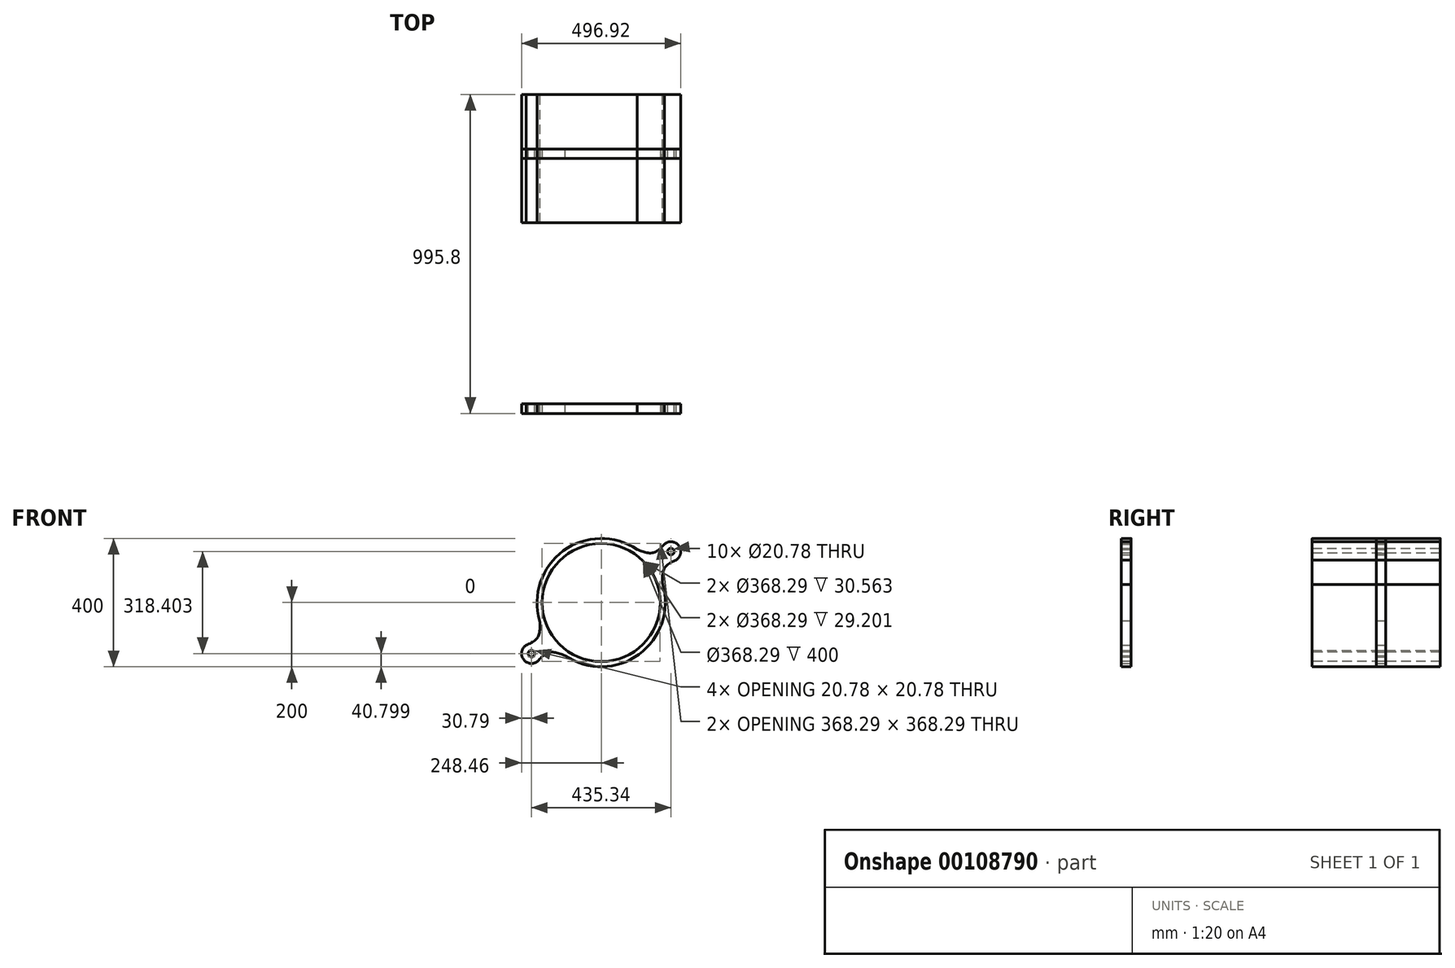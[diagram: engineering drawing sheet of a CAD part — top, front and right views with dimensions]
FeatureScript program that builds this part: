
annotation { "Feature Type Name" : "Feature", "Feature Type Description" : "" }
export const myFeature = defineFeature(function(context is Context, id is Id, definition is map)
    precondition{}
    {
        {
            var Q0;
            Q0=qCreatedBy(makeId("Front.planeOp"),FACE);
            var sketch = newSketch(context, id + "F0", { "sketchPlane" : qUnion([Q0])});
            skArc(sketch, "E0", {"start": v(111.92, 165.75) * mm, "mid": v(-118.07, 161.43) * mm, "end": v(-191.87, -56.44) * mm});
            skLineSegment(sketch, "E1", {"start": v(0, 0) * mm, "end": v(262.18, 191.76) * mm, "construction": true});
            skCircle(sketch, "E2", {"center": v(217.67, 159.2) * mm, "radius": 10.4 * mm});
            skArc(sketch, "E3.0", {"start": v(233.91, 133.04) * mm, "mid": v(242.53, 177.38) * mm, "end": v(197.66, 182.6) * mm});
            skFitSpline(sketch, "E4", {"points": [v(111.92, 165.75) * mm, v(162.07, 155.56) * mm, v(197.66, 182.6) * mm], "startDerivative": vector(103.2, -39.05) * mm, "endDerivative": vector(68, 74.26) * mm});
            skFitSpline(sketch, "E5.MirrorCS", {"points": [v(191.87, 56.44) * mm, v(197.35, 107.32) * mm, v(233.91, 133.04) * mm], "startDerivative": vector(-5.95, 110.17) * mm, "endDerivative": vector(91.37, 42.3) * mm});
            skLineSegment(sketch, "E6", {"start": v(0, 0) * mm, "end": v(0, 0) * mm});
            skLineSegment(sketch, "E7", {"start": v(0, 0) * mm, "end": v(327.07, -447.19) * mm, "construction": true});
            skFitSpline(sketch, "E8.MirrorCS", {"points": [v(-191.87, -56.44) * mm, v(-197.35, -107.32) * mm, v(-233.91, -133.04) * mm], "startDerivative": vector(5.95, -110.17) * mm, "endDerivative": vector(-91.37, -42.3) * mm});
            skArc(sketch, "E9.MirrorCS", {"start": v(-197.66, -182.6) * mm, "mid": v(-242.53, -177.38) * mm, "end": v(-233.91, -133.04) * mm});
            skFitSpline(sketch, "E10.MirrorCS", {"points": [v(-111.92, -165.75) * mm, v(-162.07, -155.56) * mm, v(-197.66, -182.6) * mm], "startDerivative": vector(-103.2, 39.05) * mm, "endDerivative": vector(-68, -74.26) * mm});
            skArc(sketch, "E11.trimOffspring", {"start": v(-111.92, -165.75) * mm, "mid": v(118.07, -161.43) * mm, "end": v(191.87, 56.44) * mm});
            skCircle(sketch, "E12.MirrorC", {"center": v(-217.67, -159.2) * mm, "radius": 10.4 * mm});
            skSolve(sketch);
        }
        {
            var Q0;
            Q0 = qSketchRegion(id + "F0", true);
            extrude(context, id + "F1", {"entities" : qUnion([Q0]), "depth" : 25 * mm});
        }
        {
            var Q0;
            Q0=makeQuery(id+"F1.opExtrude","CAP_FACE",FACE,{"disambiguationData":[OSD([sQuery(id+"F0.wireOp",EDGE,"E0"),sQuery(id+"F0.wireOp",EDGE,"E2"),sQuery(id+"F0.wireOp",EDGE,"E3.0"),sQuery(id+"F0.wireOp",EDGE,"E4"),sQuery(id+"F0.wireOp",EDGE,"E5.MirrorCS"),sQuery(id+"F0.wireOp",EDGE,"E8.MirrorCS"),sQuery(id+"F0.wireOp",EDGE,"E9.MirrorCS"),sQuery(id+"F0.wireOp",EDGE,"E10.MirrorCS"),sQuery(id+"F0.wireOp",EDGE,"E11.trimOffspring")])],"isStart":true});
            var sketch = newSketch(context, id + "F2", { "sketchPlane" : qUnion([Q0])});
            skSolve(sketch);
        }
        {
            var Q0;
            Q0 = qSketchRegion(id + "F2", true);
            var Q1;
            Q1=makeQuery(id+"F1.opExtrude","CAP_FACE",FACE,{"disambiguationData":[OSD([sQuery(id+"F0.wireOp",EDGE,"E0"),sQuery(id+"F0.wireOp",EDGE,"E2"),sQuery(id+"F0.wireOp",EDGE,"E3.0"),sQuery(id+"F0.wireOp",EDGE,"E4"),sQuery(id+"F0.wireOp",EDGE,"E5.MirrorCS"),sQuery(id+"F0.wireOp",EDGE,"E8.MirrorCS"),sQuery(id+"F0.wireOp",EDGE,"E9.MirrorCS"),sQuery(id+"F0.wireOp",EDGE,"E10.MirrorCS"),sQuery(id+"F0.wireOp",EDGE,"E11.trimOffspring")])],"isStart":false});
            extrude(context, id + "F3", {"entities" : qUnion([Q0, Q1]), "operationType" : NewBodyOperationType.ADD, "depth" : 800 * mm});
        }
        {
            var Q0;
            Q0=qCreatedBy(makeId("Top.planeOp"),FACE);
            var sketch = newSketch(context, id + "F4", { "sketchPlane" : qUnion([Q0])});
            skPoint(sketch, "E13", {"position": v(-56.15, 45.19) * mm});
            skLineSegment(sketch, "E14.bottom", {"start": v(288.67, -29.2) * mm, "end": v(-332.07, -29.2) * mm});
            skLineSegment(sketch, "E14.top", {"start": v(288.67, -794.44) * mm, "end": v(-332.07, -794.44) * mm});
            skLineSegment(sketch, "E14.left", {"start": v(288.67, -29.2) * mm, "end": v(288.67, -794.44) * mm});
            skLineSegment(sketch, "E14.right", {"start": v(-332.07, -29.2) * mm, "end": v(-332.07, -794.44) * mm});
            skSolve(sketch);
        }
        {
            var Q0;
            Q0 = qSketchRegion(id + "F4", true);
            extrude(context, id + "F5", {"entities" : qUnion([Q0]), "operationType" : NewBodyOperationType.REMOVE, "endBound" : BoundingType.SYMMETRIC, "oppositeDirection" : true, "depth" : 578.57 * mm});
        }
        {
            var Q0;
            Q0=makeQuery(id+"F5.boolean.opBoolean","SPLIT",BODY,{"disambiguationData":[OD(0.0)],"derivedFrom":makeQuery(id+"F1.opExtrude","SWEPT_BODY",BODY,{"disambiguationData":[OSD([sQuery(id+"F0.wireOp",EDGE,"E0"),sQuery(id+"F0.wireOp",EDGE,"E2"),sQuery(id+"F0.wireOp",EDGE,"E3.0"),sQuery(id+"F0.wireOp",EDGE,"E4"),sQuery(id+"F0.wireOp",EDGE,"E5.MirrorCS"),sQuery(id+"F0.wireOp",EDGE,"E8.MirrorCS"),sQuery(id+"F0.wireOp",EDGE,"E9.MirrorCS"),sQuery(id+"F0.wireOp",EDGE,"E10.MirrorCS"),sQuery(id+"F0.wireOp",EDGE,"E11.trimOffspring"),sQuery(id+"F0.wireOp",EDGE,"E12.MirrorC")])]})});
            transform(context, id + "F6", {"entities" : qUnion([Q0]), "transformType" : TransformType.TRANSLATION_3D, "dx" : 0 * mm, "dy" : 0 * mm, "dz" : 0 * mm, "makeCopy" : true});
        }
        {
            var Q0;
            Q0=makeQuery(id+"F5.boolean.opBoolean","COPY",FACE,{"derivedFrom":makeQuery(id+"F5.opExtrude","SWEPT_FACE",FACE,{"disambiguationData":[OSD([sQuery(id+"F4.wireOp",EDGE,"E14.bottom")])]})});
            var sketch = newSketch(context, id + "F7", { "sketchPlane" : qUnion([Q0])});
            skSolve(sketch);
        }
        {
            var Q0;
            {var subQ0=makeQuery(id+"F5.opExtrude","SWEPT_FACE",FACE,{"disambiguationData":[OSD([sQuery(id+"F4.wireOp",EDGE,"E14.bottom")])]});var subQ4=sQuery(id+"F0.wireOp",EDGE,"E2");Q0=makeQuery(id+"F7.imprint","IMPRINT",FACE,{"disambiguationData":[TD([[makeQuery(id+"F7.imprint","IMPRINT",EDGE,{"derivedFrom":makeQuery(id+"F5.boolean.opBoolean","INTERSECT",EDGE,{"derivedFrom":[makeQuery(id+"F3.boolean.opBoolean","MERGE",FACE,{"derivedFrom":[makeQuery(id+"F1.opExtrude","SWEPT_FACE",FACE,{"disambiguationData":[OSD([subQ4])]}),makeQuery(id+"F3.opExtrude","SWEPT_FACE",FACE,{"disambiguationData":[OSD([subQ4])]})]}),subQ0]})}),1.0]])]});}
            extrude(context, id + "F8", {"entities" : qUnion([Q0]), "endBound" : BoundingType.SYMMETRIC, "depth" : 400 * mm});
        }
        {
            var Q0;
            Q0=makeQuery(id+"F8.opExtrude","CAP_FACE",FACE,{"disambiguationData":[OSD([sQuery(id+"F0.wireOp",EDGE,"E0"),sQuery(id+"F0.wireOp",EDGE,"E2"),sQuery(id+"F0.wireOp",EDGE,"E3.0"),sQuery(id+"F0.wireOp",EDGE,"E4"),sQuery(id+"F0.wireOp",EDGE,"E5.MirrorCS"),sQuery(id+"F0.wireOp",EDGE,"E8.MirrorCS"),sQuery(id+"F0.wireOp",EDGE,"E9.MirrorCS"),sQuery(id+"F0.wireOp",EDGE,"E10.MirrorCS"),sQuery(id+"F0.wireOp",EDGE,"E11.trimOffspring"),sQuery(id+"F0.wireOp",EDGE,"E12.MirrorC"),sQuery(id+"F4.wireOp",EDGE,"E14.bottom")])],"isStart":false});
            var sketch = newSketch(context, id + "F9", { "sketchPlane" : qUnion([Q0])});
            skCircle(sketch, "E15", {"center": v(0, 0) * mm, "radius": 184.15 * mm});
            skSolve(sketch);
        }
        {
            var Q0;
            Q0 = qSketchRegion(id + "F9", true);
            extrude(context, id + "F10", {"entities" : qUnion([Q0]), "operationType" : NewBodyOperationType.REMOVE, "endBound" : BoundingType.SYMMETRIC, "oppositeDirection" : true, "depth" : 2000 * mm});
        }
    });
